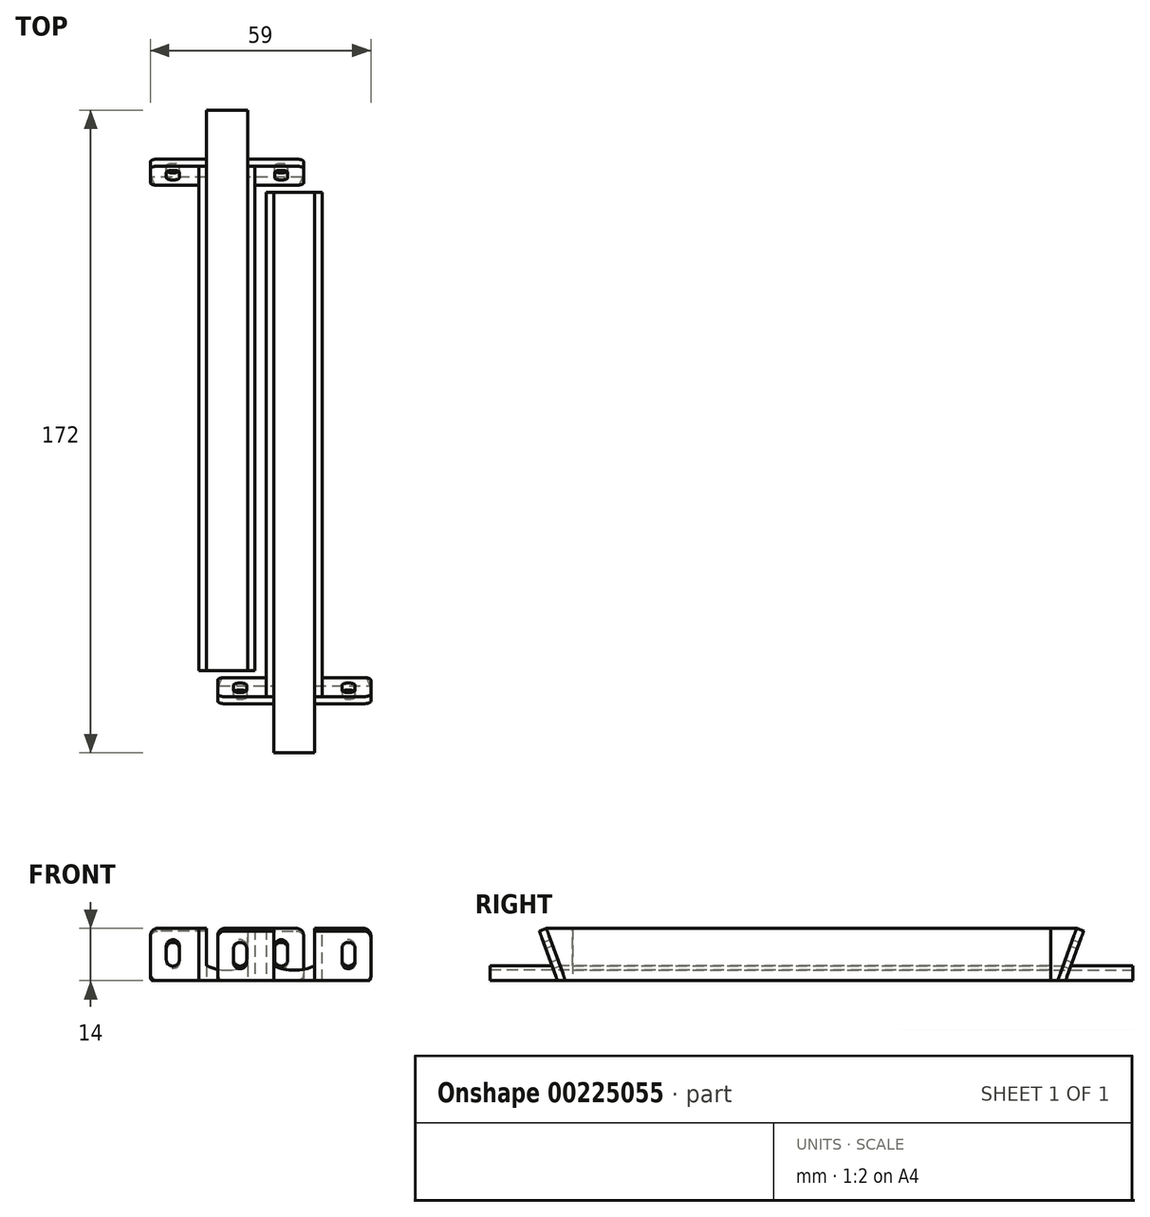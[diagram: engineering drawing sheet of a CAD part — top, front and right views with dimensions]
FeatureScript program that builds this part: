
annotation { "Feature Type Name" : "Feature", "Feature Type Description" : "" }
export const myFeature = defineFeature(function(context is Context, id is Id, definition is map)
    precondition{}
    {
        {
            var Q0;
            Q0=qCreatedBy(makeId("Front.planeOp"),FACE);
            var sketch = newSketch(context, id + "F0", { "sketchPlane" : qUnion([Q0])});
            skLineSegment(sketch, "E0.bottom", {"start": v(-7.5, 14) * mm, "end": v(-5.5, 14) * mm});
            skLineSegment(sketch, "E0.top", {"start": v(-7.5, 0) * mm, "end": v(7.5, 0) * mm});
            skLineSegment(sketch, "E0.left", {"start": v(-7.5, 14) * mm, "end": v(-7.5, 0) * mm});
            skLineSegment(sketch, "E0.right", {"start": v(7.5, 14) * mm, "end": v(7.5, 0) * mm});
            skLineSegment(sketch, "E1", {"start": v(-5.5, 14) * mm, "end": v(-5.5, 4) * mm});
            skLineSegment(sketch, "E2", {"start": v(5.5, 4) * mm, "end": v(5.5, 14) * mm});
            skLineSegment(sketch, "E3.trimOffspring", {"start": v(5.5, 14) * mm, "end": v(7.5, 14) * mm});
            skArc(sketch, "E4", {"start": v(-5.5, 4) * mm, "mid": v(0, 2.78) * mm, "end": v(5.5, 4) * mm});
            skSolve(sketch);
        }
        {
            var Q0;
            Q0=qSketchRegion(id+"F0",true);
            extrude(context, id + "F1", {"entities" : qUnion([Q0]), "depth" : 150 * mm});
        }
        {
            var Q0;
            Q0=makeQuery(id+"F1.opExtrude","SWEPT_FACE",FACE,{"disambiguationData":[OSD([sQuery(id+"F0.wireOp",EDGE,"E0.left")])]});
            var sketch = newSketch(context, id + "F2", { "sketchPlane" : qUnion([Q0])});
            skLineSegment(sketch, "E5", {"start": v(18.64, 4) * mm, "end": v(15, 14) * mm});
            skLineSegment(sketch, "E6", {"start": v(15, 14) * mm, "end": v(15, 4) * mm});
            skLineSegment(sketch, "E7", {"start": v(15, 4) * mm, "end": v(18.64, 4) * mm});
            skLineSegment(sketch, "E8.bottom", {"start": v(15, 14) * mm, "end": v(-5, 14) * mm});
            skLineSegment(sketch, "E8.top", {"start": v(15, 4) * mm, "end": v(-5, 4) * mm});
            skLineSegment(sketch, "E8.right", {"start": v(-5, 14) * mm, "end": v(-5, 4) * mm});
            skSolve(sketch);
        }
        {
            var Q0;
            Q0=qSketchRegion(id+"F2",true);
            extrude(context, id + "F3", {"entities" : qUnion([Q0]), "operationType" : NewBodyOperationType.REMOVE, "oppositeDirection" : true, "depth" : 25 * mm});
        }
        {
            var Q0;
            Q0=makeQuery(id+"F3.boolean.opBoolean","COPY",FACE,{"disambiguationData":[TD([makeQuery(id+"F1.opExtrude","SWEPT_FACE",FACE,{"disambiguationData":[OSD([sQuery(id+"F0.wireOp",EDGE,"E0.bottom")])]})])],"derivedFrom":makeQuery(id+"F3.opExtrude","SWEPT_FACE",FACE,{"disambiguationData":[OSD([sQuery(id+"F2.wireOp",EDGE,"E5")])]})});
            var sketch = newSketch(context, id + "F4", { "sketchPlane" : qUnion([Q0])});
            skLineSegment(sketch, "E9.bottom", {"start": v(5.5, 8.03) * mm, "end": v(20.5, 8.03) * mm});
            skLineSegment(sketch, "E9.top", {"start": v(5.5, -6.97) * mm, "end": v(20.5, -6.97) * mm});
            skLineSegment(sketch, "E9.left", {"start": v(5.5, 8.03) * mm, "end": v(5.5, -6.97) * mm});
            skLineSegment(sketch, "E9.right", {"start": v(20.5, 8.03) * mm, "end": v(20.5, -6.97) * mm});
            skLineSegment(sketch, "E10.bottom", {"start": v(-5.5, 8.03) * mm, "end": v(-20.5, 8.03) * mm});
            skLineSegment(sketch, "E10.top", {"start": v(-5.5, -6.97) * mm, "end": v(-20.5, -6.97) * mm});
            skLineSegment(sketch, "E10.left", {"start": v(-5.5, 8.03) * mm, "end": v(-5.5, -6.97) * mm});
            skLineSegment(sketch, "E10.right", {"start": v(-20.5, 8.03) * mm, "end": v(-20.5, -6.97) * mm});
            skSolve(sketch);
        }
        {
            var Q0;
            Q0=qSketchRegion(id+"F4",true);
            extrude(context, id + "F5", {"entities" : qUnion([Q0]), "operationType" : NewBodyOperationType.ADD, "depth" : 2 * mm});
        }
        {
            var Q0;
            Q0=makeQuery(id+"F5.opExtrude","SWEPT_EDGE",EDGE,{"disambiguationData":[OSD([sQuery(id+"F4.wireOp",EDGE,"E10.bottom"),sQuery(id+"F4.wireOp",EDGE,"E10.right")])]});
            var Q1;
            Q1=makeQuery(id+"F5.opExtrude","SWEPT_EDGE",EDGE,{"disambiguationData":[OSD([sQuery(id+"F4.wireOp",EDGE,"E9.bottom"),sQuery(id+"F4.wireOp",EDGE,"E9.right")])]});
            var Q2;
            Q2=makeQuery(id+"F5.opExtrude","SWEPT_EDGE",EDGE,{"disambiguationData":[OSD([sQuery(id+"F4.wireOp",EDGE,"E10.top"),sQuery(id+"F4.wireOp",EDGE,"E10.right")])]});
            var Q3;
            Q3=makeQuery(id+"F5.opExtrude","SWEPT_EDGE",EDGE,{"disambiguationData":[OSD([sQuery(id+"F4.wireOp",EDGE,"E9.top"),sQuery(id+"F4.wireOp",EDGE,"E9.right")])]});
            fillet(context, id + "F6", {"entities" : qUnion([Q0, Q1, Q2, Q3]), "radius" : 2 * mm, "tangentPropagation" : true, "allowEdgeOverflow" : false});
        }
        {
            var Q0;
            Q0=makeQuery(id+"F1.opExtrude","SWEPT_FACE",FACE,{"disambiguationData":[OSD([sQuery(id+"F0.wireOp",EDGE,"E0.top")])]});
            var sketch = newSketch(context, id + "F7", { "sketchPlane" : qUnion([Q0])});
            skLineSegment(sketch, "E11.bottom", {"start": v(28.06, 12.59) * mm, "end": v(-35.23, 12.59) * mm});
            skLineSegment(sketch, "E11.top", {"start": v(28.06, 27.5) * mm, "end": v(-35.23, 27.5) * mm});
            skLineSegment(sketch, "E11.left", {"start": v(28.06, 12.59) * mm, "end": v(28.06, 27.5) * mm});
            skLineSegment(sketch, "E11.right", {"start": v(-35.23, 12.59) * mm, "end": v(-35.23, 27.5) * mm});
            skSolve(sketch);
        }
        {
            var Q0;
            Q0 = qSketchRegion(id + "F7", true);
            extrude(context, id + "F8", {"entities" : qUnion([Q0]), "operationType" : NewBodyOperationType.REMOVE, "depth" : 100 * mm});
        }
        {
            var Q0;
            Q0=makeQuery(id+"F5.opExtrude","CAP_FACE",FACE,{"disambiguationData":[OSD([sQuery(id+"F4.wireOp",EDGE,"E9.bottom"),sQuery(id+"F4.wireOp",EDGE,"E9.top"),sQuery(id+"F4.wireOp",EDGE,"E9.left"),sQuery(id+"F4.wireOp",EDGE,"E9.right")])],"isStart":false});
            var sketch = newSketch(context, id + "F9", { "sketchPlane" : qUnion([Q0])});
            skArc(sketch, "E12", {"start": v(16.25, 3) * mm, "mid": v(14.52, 4.78) * mm, "end": v(12.75, 3.03) * mm});
            skArc(sketch, "E13", {"start": v(12.75, -0.97) * mm, "mid": v(14.52, -2.72) * mm, "end": v(16.25, -0.94) * mm});
            skLineSegment(sketch, "E14", {"start": v(16.25, 3.06) * mm, "end": v(16.25, -0.97) * mm});
            skLineSegment(sketch, "E15", {"start": v(12.75, -0.97) * mm, "end": v(12.75, 3.03) * mm});
            skLineSegment(sketch, "E16.MirrorCS", {"start": v(-12.75, -0.97) * mm, "end": v(-12.75, 3.03) * mm});
            skLineSegment(sketch, "E17.MirrorCS", {"start": v(-16.25, 3.06) * mm, "end": v(-16.25, -0.97) * mm});
            skArc(sketch, "E18.MirrorCS", {"start": v(-12.75, -0.97) * mm, "mid": v(-14.52, -2.72) * mm, "end": v(-16.25, -0.94) * mm});
            skArc(sketch, "E19.MirrorCS", {"start": v(-16.25, 3) * mm, "mid": v(-14.52, 4.78) * mm, "end": v(-12.75, 3.03) * mm});
            skSolve(sketch);
        }
        {
            var Q0;
            Q0 = qSketchRegion(id + "F9", true);
            extrude(context, id + "F10", {"entities" : qUnion([Q0]), "operationType" : NewBodyOperationType.REMOVE, "oppositeDirection" : true, "depth" : 25 * mm});
        }
        {
            var Q0;
            {var subQ2=sQuery(id+"F0.wireOp",EDGE,"E0.right");var subQ5=makeQuery(id+"F1.opExtrude","SWEPT_FACE",FACE,{"disambiguationData":[OSD([subQ2])]});Q0=makeQuery(id+"F5.boolean.opBoolean","SPLIT",FACE,{"disambiguationData":[TD([makeQuery(id+"F5.opExtrude","CAP_FACE",FACE,{"disambiguationData":[OSD([sQuery(id+"F4.wireOp",EDGE,"E10.bottom"),sQuery(id+"F4.wireOp",EDGE,"E10.top"),sQuery(id+"F4.wireOp",EDGE,"E10.left"),sQuery(id+"F4.wireOp",EDGE,"E10.right")])],"isStart":false})])],"derivedFrom":subQ5});}
            var sketch = newSketch(context, id + "F11", { "sketchPlane" : qUnion([Q0])});
            skLineSegment(sketch, "E20", {"start": v(-16.51, 4) * mm, "end": v(-17.97, 0) * mm});
            skLineSegment(sketch, "E21", {"start": v(-17.97, 0) * mm, "end": v(0, 0) * mm});
            skLineSegment(sketch, "E22", {"start": v(0, 0) * mm, "end": v(0, 4) * mm});
            skLineSegment(sketch, "E23", {"start": v(0, 4) * mm, "end": v(-16.51, 4) * mm});
            skSolve(sketch);
        }
        {
            var Q0;
            Q0 = qSketchRegion(id + "F11", true);
            extrude(context, id + "F12", {"entities" : qUnion([Q0]), "operationType" : NewBodyOperationType.REMOVE, "oppositeDirection" : true, "depth" : 2 * mm});
        }
        {
            var Q0;
            {var subQ2=sQuery(id+"F0.wireOp",EDGE,"E0.left");var subQ5=makeQuery(id+"F1.opExtrude","SWEPT_FACE",FACE,{"disambiguationData":[OSD([subQ2])]});Q0=makeQuery(id+"F5.boolean.opBoolean","SPLIT",FACE,{"disambiguationData":[TD([makeQuery(id+"F5.opExtrude","CAP_FACE",FACE,{"disambiguationData":[OSD([sQuery(id+"F4.wireOp",EDGE,"E9.bottom"),sQuery(id+"F4.wireOp",EDGE,"E9.top"),sQuery(id+"F4.wireOp",EDGE,"E9.left"),sQuery(id+"F4.wireOp",EDGE,"E9.right")])],"isStart":false})])],"derivedFrom":subQ5});}
            var sketch = newSketch(context, id + "F13", { "sketchPlane" : qUnion([Q0])});
            skLineSegment(sketch, "E24", {"start": v(0, 4) * mm, "end": v(16.51, 4) * mm});
            skLineSegment(sketch, "E25", {"start": v(16.51, 4) * mm, "end": v(17.97, 0) * mm});
            skLineSegment(sketch, "E26", {"start": v(17.97, 0) * mm, "end": v(0, 0) * mm});
            skLineSegment(sketch, "E27", {"start": v(0, 0) * mm, "end": v(0, 4) * mm});
            skSolve(sketch);
        }
        {
            var Q0;
            Q0 = qSketchRegion(id + "F13", true);
            extrude(context, id + "F14", {"entities" : qUnion([Q0]), "operationType" : NewBodyOperationType.REMOVE, "oppositeDirection" : true, "depth" : 2 * mm});
        }
        {
            var Q0;
            Q0=makeQuery(id+"F1.opExtrude","SWEPT_BODY",BODY,{"disambiguationData":[OSD([sQuery(id+"F0.wireOp",EDGE,"E0.bottom"),sQuery(id+"F0.wireOp",EDGE,"E0.top"),sQuery(id+"F0.wireOp",EDGE,"E0.left"),sQuery(id+"F0.wireOp",EDGE,"E0.right"),sQuery(id+"F0.wireOp",EDGE,"E1"),sQuery(id+"F0.wireOp",EDGE,"E2"),sQuery(id+"F0.wireOp",EDGE,"E3.trimOffspring"),sQuery(id+"F0.wireOp",EDGE,"E4")])]});
            var Q1;
            Q1=makeQuery(id+"F1.opExtrude","CAP_EDGE",EDGE,{"disambiguationData":[OSD([sQuery(id+"F0.wireOp",EDGE,"E0.right")])],"isStart":false});
            transform(context, id + "F15", {"entities" : qUnion([Q0]), "transformType" : TransformType.ROTATION, "transformAxis" : qUnion([Q1]), "angle" : 180 * degree, "makeCopy" : true});
        }
        {
            var Q0;
            Q0=makeQuery(id+"F15.opPattern","COPY",BODY,{"derivedFrom":makeQuery(id+"F1.opExtrude","SWEPT_BODY",BODY,{"disambiguationData":[OSD([sQuery(id+"F0.wireOp",EDGE,"E0.bottom"),sQuery(id+"F0.wireOp",EDGE,"E0.top"),sQuery(id+"F0.wireOp",EDGE,"E0.left"),sQuery(id+"F0.wireOp",EDGE,"E0.right"),sQuery(id+"F0.wireOp",EDGE,"E1"),sQuery(id+"F0.wireOp",EDGE,"E2"),sQuery(id+"F0.wireOp",EDGE,"E3.trimOffspring"),sQuery(id+"F0.wireOp",EDGE,"E4")])]}),"instanceName":"1"});
            transform(context, id + "F16", {"entities" : qUnion([Q0]), "transformType" : TransformType.TRANSLATION_3D, "dx" : 3 * mm, "dy" : 128 * mm, "dz" : 0 * mm, "makeCopy" : false});
        }
    });
